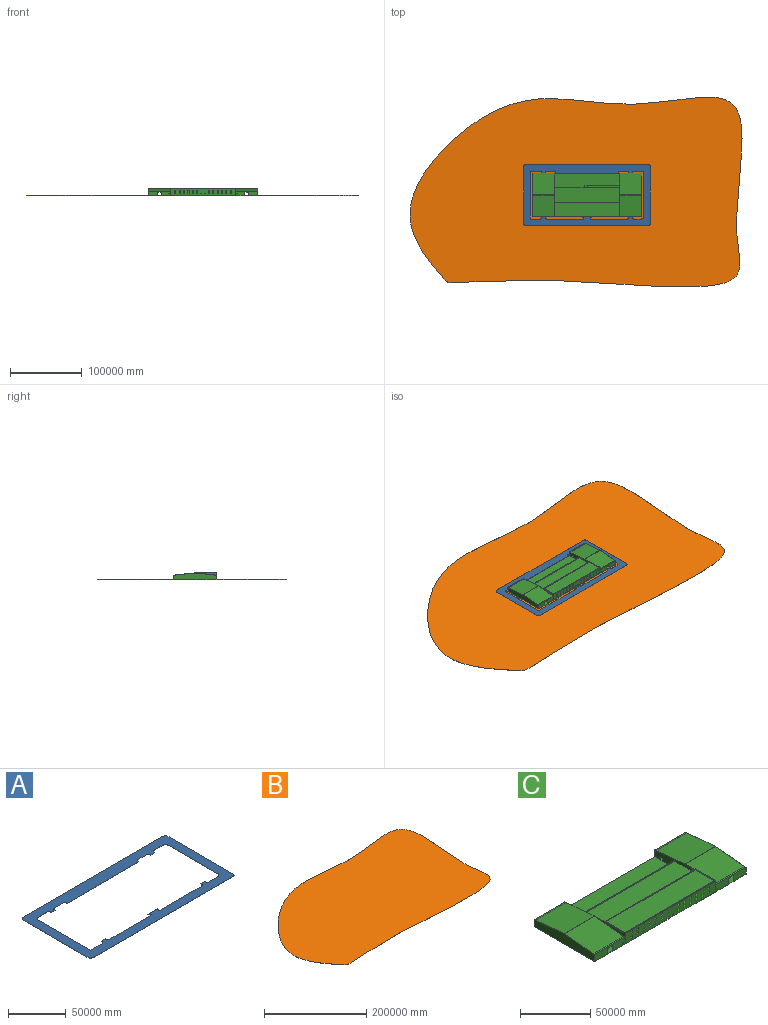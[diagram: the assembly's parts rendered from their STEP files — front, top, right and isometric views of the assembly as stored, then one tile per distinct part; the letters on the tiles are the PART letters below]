
ASSEMBLY  parts=3 mates=2
PART A: 50 faces, bbox 176784x85344x152.4 mm
  f0: plane 52273.2x152.4mm, normal (0,1,0), area 7966435.7mm2, adj f1,f47,f48,f49
  f1: cylinder r=3810mm len=3048mm, axis (0,0,-1), area 538428.4mm2, adj f0,f2,f48,f49
  f2: plane 12192x152.4mm, normal (0,1,0), area 1858060.8mm2, adj f1,f3,f48,f49
  f3: cylinder r=3810mm len=3048mm, axis (0,0,-1), area 538428.4mm2, adj f2,f4,f48,f49
  f4: plane 52273.2x152.4mm, normal (0,1,0), area 7966435.7mm2, adj f3,f5,f48,f49
  f5: plane 152.4x152.4mm, normal (1,0,0), area 23225.8mm2, adj f4,f6,f48,f49
  f6: extruded ~2895.6x1524mm, area 548894mm2, adj f5,f7,f48,f49
  f7: plane 152.4x152.4mm, normal (1,0,0), area 23225.8mm2, adj f6,f8,f48,f49
  f8: plane 4876.8x152.4mm, normal (0,1,0), area 743224.3mm2, adj f7,f9,f48,f49
  f9: plane 152.4x152.4mm, normal (-1,0,0), area 23225.8mm2, adj f8,f10,f48,f49
  f10: extruded ~2895.6x1524mm, area 548894mm2, adj f9,f11,f48,f49
  f11: plane 152.4x152.4mm, normal (-1,0,0), area 23225.8mm2, adj f10,f12,f48,f49
  f12: plane 14478x152.4mm, normal (0,1,0), area 2206447.2mm2, adj f11,f13,f48,f49
  f13: plane 63855.6x152.4mm, normal (1,0,0), area 9731593.4mm2, adj f12,f14,f48,f49
  f14: cylinder r=3048mm len=3048mm, axis (0,0,-1), area 729658.8mm2, adj f13,f15,f48,f49
  f15: plane 11430x152.4mm, normal (0,-1,0), area 1741932mm2, adj f14,f16,f48,f49
  f16: extruded ~2895.6x1524mm, area 548894mm2, adj f15,f17,f48,f49
  f17: plane 4876.8x152.4mm, normal (0,-1,0), area 743224.3mm2, adj f16,f18,f48,f49
  f18: extruded ~2895.6x1524mm, area 548894mm2, adj f17,f19,f48,f49
  f19: plane 11430x152.4mm, normal (0,-1,0), area 1741932mm2, adj f18,f20,f48,f49
  f20: extruded ~2895.6x1524mm, area 548894mm2, adj f19,f21,f48,f49
  f21: plane 87782.4x152.4mm, normal (0,-1,0), area 13378037.8mm2, adj f20,f22,f48,f49
  f22: extruded ~2895.6x1524mm, area 548894mm2, adj f21,f23,f48,f49
  f23: plane 11430x152.4mm, normal (0,-1,0), area 1741932mm2, adj f22,f24,f48,f49
  f24: extruded ~2895.6x1524mm, area 548894mm2, adj f23,f25,f48,f49
  f25: plane 4876.8x152.4mm, normal (0,-1,0), area 743224.3mm2, adj f24,f26,f48,f49
  f26: extruded ~2895.6x1524mm, area 548894mm2, adj f25,f27,f48,f49
  f27: plane 11430x152.4mm, normal (0,-1,0), area 1741932mm2, adj f26,f28,f48,f49
  f28: cylinder r=3048mm len=3048mm, axis (0,0,-1), area 729658.8mm2, adj f27,f29,f48,f49
  f29: plane 60655.2x152.4mm, normal (-1,0,0), area 9243852.5mm2, adj f28,f30,f48,f49
  f30: cylinder r=3048mm len=3048mm, axis (0,0,-1), area 729658.8mm2, adj f29,f31,f48,f49
  f31: plane 296.88x152.4mm, normal (-0.46,0.89,0), area 50857.4mm2, adj f30,f32,f48,f49
  f32: plane 11133.12x152.4mm, normal (0,1,0), area 1696687.8mm2, adj f31,f33,f48,f49
  f33: plane 152.4x152.4mm, normal (1,0,0), area 23225.8mm2, adj f32,f34,f48,f49
  f34: extruded ~2895.6x1524mm, area 548894mm2, adj f33,f35,f48,f49
  f35: plane 152.4x152.4mm, normal (1,0,0), area 23225.8mm2, adj f34,f36,f48,f49
  f36: plane 4876.8x152.4mm, normal (0,1,0), area 743224.3mm2, adj f35,f37,f48,f49
  f37: plane 152.4x152.4mm, normal (-1,0,0), area 23225.8mm2, adj f36,f38,f48,f49
  f38: extruded ~2895.6x1524mm, area 548894mm2, adj f37,f47,f48,f49
  f39: cylinder r=3048mm len=3048mm, axis (0,0,-1), area 729658.8mm2, adj f40,f46,f48,f49
  f40: plane 79248x152.4mm, normal (-1,0,0), area 12077395.2mm2, adj f39,f41,f48,f49
  f41: cylinder r=3048mm len=3048mm, axis (0,0,-1), area 729658.8mm2, adj f40,f42,f48,f49
  f42: plane 170688x152.4mm, normal (0,-1,0), area 26012851.2mm2, adj f41,f43,f48,f49
  f43: cylinder r=3048mm len=3048mm, axis (0,0,-1), area 729658.8mm2, adj f42,f44,f48,f49
  f44: plane 79248x152.4mm, normal (1,0,0), area 12077395.2mm2, adj f43,f45,f48,f49
  f45: cylinder r=3048mm len=3048mm, axis (0,0,-1), area 729658.8mm2, adj f44,f46,f48,f49
  f46: plane 170688x152.4mm, normal (0,1,0), area 26012851.2mm2, adj f39,f45,f48,f49
  f47: plane 152.4x152.4mm, normal (-1,0,0), area 23225.8mm2, adj f0,f38,f48,f49
  f48: plane 176784x85344mm, normal (0,0,1), area 4835317142.7mm2, adj f0,f1,f2,f3,f4,f5,f6,f7
  f49: plane 176784x85344mm, normal (0,0,-1), area 4835317142.7mm2, adj f0,f1,f2,f3,f4,f5,f6,f7
PART B: 3 faces, bbox 484095.1x286229.5x152.4 mm
  f0: extruded ~463355.35x265089.78mm, area 197646729.1mm2, adj f1,f2
  f1: plane 484095.12x286229.54mm, normal (0,0,1), area 107619152250.1mm2, adj f0
  f2: plane 484095.12x286229.54mm, normal (0,0,-1), area 107619152250.1mm2, adj f0
PART C: 253 faces, bbox 152400x60960x9906 mm
  f0: plane 30480x5943.6mm, normal (0,-1,0), area 158120974.1mm2, adj f3,f168,f172,f179,f250,f251,f252
  f1: plane 30480x5943.6mm, normal (0,-1,0), area 158120974.1mm2, adj f4,f169,f172,f177,f246,f247,f248
  f2: plane 40843.2x9144mm, normal (1,0,0), area 189846781.6mm2, adj f5,f8,f10,f12,f17,f18,f27,f28
  f3: plane 60655.2x8839.2mm, normal (-1,0,0), area 317727235.5mm2, adj f0,f6,f167,f171,f172,f173,f179,f180
  f4: plane 60655.2x8839.2mm, normal (1,0,0), area 317727235.5mm2, adj f1,f6,f170,f171,f172,f173,f174,f175
  f5: plane 90830.4x7010.4mm, normal (0,1,0), area 589934303.9mm2, adj f2,f13,f31,f35,f172,f184,f236,f237
  f6: plane 91135.2x5943.6mm, normal (0,-1,0), area 537769247mm2, adj f3,f4,f172,f173,f236,f237,f238
  f7: plane 90830.4x8991.6mm, normal (0,-1,0), area 784937785mm2, adj f12,f163,f164,f165,f166,f185,f186,f187
  f8: plane 91135.2x3657.6mm, normal (0,1,0), area 300680689mm2, adj f2,f10,f11,f12,f13,f24,f25,f40
  f9: plane 152400x9906mm, normal (0,-1,0), area 1161241548.5mm2, adj f17,f19,f20,f22,f23,f24,f25,f40
  f10: plane 30784.8x10515.6mm, normal (0,0,1), area 10939333mm2, adj f2,f8,f19,f20,f25,f28
  f11: plane 30784.8x10515.6mm, normal (0,0,1), area 10939333mm2, adj f8,f13,f21,f22,f23,f24
  f12: plane 90830.4x20878.8mm, normal (0,0,1), area 1882865911.7mm2, adj f2,f7,f8,f13,f34,f186,f187
  f13: plane 40843.2x9144mm, normal (-1,0,0), area 185666144.8mm2, adj f5,f8,f11,f12,f15,f16,f17,f18
  f14: plane 1516.38x152.4mm, normal (1,0,0), area 115548.2mm2, adj f15,f16,f21
  f15: plane 30784.8x6248.4mm, normal (0,1,0), area 163904188.3mm2, adj f13,f14,f16,f17,f21,f22,f246,f247
  f16: plane 1516.38x152.4mm, normal (0,0,1), area 231096.3mm2, adj f13,f14,f15,f21
  f17: plane 152400x60960mm, normal (0,0,-1), area 9272652422.4mm2, adj f2,f9,f13,f15,f18,f20,f22,f27
  f18: plane 90830.4x152.4mm, normal (0,1,0), area 13842553mm2, adj f2,f13,f17,f172
  f19: plane 30632.4x30327.6mm, normal (0,-0.1,0.99), area 933687222.9mm2, adj f9,f10,f20,f25
  f20: plane 60960x9144mm, normal (-1,0,0), area 464979715.2mm2, adj f9,f10,f17,f19,f27,f28
  f21: plane 30784.8x30327.6mm, normal (0,0.1,0.99), area 938100172.4mm2, adj f11,f13,f14,f15,f16,f22
  f22: plane 60960x9144mm, normal (1,0,0), area 464979715.2mm2, adj f9,f11,f15,f17,f21,f23
  f23: plane 30632.4x30327.6mm, normal (0,-0.1,0.99), area 933687222.9mm2, adj f9,f11,f22,f24
  f24: plane 30327.6x3810mm, normal (1,0,0), area 61548264mm2, adj f8,f9,f11,f23,f40
  f25: plane 30327.6x3810mm, normal (-1,0,0), area 61548264mm2, adj f8,f9,f10,f19,f40
  f26: plane 1516.38x152.4mm, normal (-1,0,0), area 115548.2mm2, adj f27,f28,f29
  f27: plane 30784.8x6248.4mm, normal (0,1,0), area 163904188.3mm2, adj f2,f17,f20,f26,f28,f29,f250,f251
  f28: plane 30784.8x30327.6mm, normal (0,0.1,0.99), area 938100172.4mm2, adj f2,f10,f20,f26,f27,f29
  f29: plane 1516.38x152.4mm, normal (0,0,1), area 231096.3mm2, adj f2,f26,f27,f28
  f30: plane 45415.2x914.4mm, normal (0,1,0), area 40134113.3mm2, adj f31,f33,f172,f184
  f31: plane 45415.2x3048mm, normal (0,0,1), area 138425529.6mm2, adj f5,f13,f30,f32,f184
  f32: plane 3048x3048mm, normal (0,0.29,0.96), area 9699362.1mm2, adj f13,f31,f33,f172
  f33: plane 3048x914.4mm, normal (-1,0,0), area 1393545.6mm2, adj f30,f32,f172
  f34: plane 90830.4x914.4mm, normal (0,-1,0), area 83055317.8mm2, adj f2,f12,f13,f35
  f35: plane 90830.4x152.4mm, normal (0,0,1), area 13842553mm2, adj f2,f5,f13,f34
  f36: plane 90525.6x609.6mm, normal (0,1,0), area 55184405.8mm2, adj f37,f39,f40,f41
  f37: plane 19507.2x609.6mm, normal (1,0,0), area 11891589.1mm2, adj f36,f38,f40,f41
  f38: plane 90525.6x609.6mm, normal (0,-1,0), area 55184405.8mm2, adj f37,f39,f40,f41
  f39: plane 19507.2x609.6mm, normal (-1,0,0), area 11891589.1mm2, adj f36,f38,f40,f41
  f40: plane 91135.2x20116.8mm, normal (0,0,1), area 67447607mm2, adj f8,f9,f24,f25,f36,f37,f38,f39
  f41: plane 90525.6x19507.2mm, normal (0,0,1), area 1765900984.3mm2, adj f36,f37,f38,f39
  f42: plane 4876.8x152.4mm, normal (-1,0,0), area 743224.3mm2, adj f9,f17,f43,f45,f170
  f43: plane 4876.8x152.4mm, normal (0,0,-1), area 743224.3mm2, adj f9,f42,f44,f170
  f44: plane 4876.8x152.4mm, normal (1,0,0), area 743224.3mm2, adj f9,f17,f43,f45,f170
  f45: plane 4876.8x152.4mm, normal (0,-1,0), area 743224.3mm2, adj f17,f42,f44,f172
  f46: plane 2133.6x152.4mm, normal (-1,0,0), area 325160.6mm2, adj f9,f17,f47,f49,f170
  f47: plane 914.4x152.4mm, normal (0,0,-1), area 139354.6mm2, adj f9,f46,f48,f170
  f48: plane 2133.6x152.4mm, normal (1,0,0), area 325160.6mm2, adj f9,f17,f47,f49,f170
  f49: plane 914.4x152.4mm, normal (0,-1,0), area 139354.6mm2, adj f17,f46,f48,f172
  f50: plane 2133.6x152.4mm, normal (1,0,0), area 325160.6mm2, adj f9,f17,f52,f53,f167
  f51: plane 2133.6x152.4mm, normal (-1,0,0), area 325160.6mm2, adj f9,f17,f52,f53,f167
  f52: plane 914.4x152.4mm, normal (0,0,-1), area 139354.6mm2, adj f9,f50,f51,f167
  f53: plane 914.4x152.4mm, normal (0,-1,0), area 139354.6mm2, adj f17,f50,f51,f172
  f54: plane 4876.8x152.4mm, normal (0,0,-1), area 743224.3mm2, adj f9,f55,f56,f167
  f55: plane 4876.8x152.4mm, normal (1,0,0), area 743224.3mm2, adj f9,f17,f54,f57,f167
  f56: plane 4876.8x152.4mm, normal (-1,0,0), area 743224.3mm2, adj f9,f17,f54,f57,f167
  f57: plane 4876.8x152.4mm, normal (0,-1,0), area 743224.3mm2, adj f17,f55,f56,f172
  f58: plane 2133.6x152.4mm, normal (1,0,0), area 325160.6mm2, adj f9,f17,f60,f61,f162
  f59: plane 2133.6x152.4mm, normal (-1,0,0), area 325160.6mm2, adj f9,f17,f60,f61,f162
  f60: plane 1828.8x152.4mm, normal (0,0,-1), area 278709.1mm2, adj f9,f58,f59,f162
  f61: plane 1828.8x152.4mm, normal (0,-1,0), area 278709.1mm2, adj f17,f58,f59,f163
  f62: plane 1524x152.4mm, normal (-1,0,0), area 232257.6mm2, adj f9,f63,f65,f162
  f63: plane 1524x152.4mm, normal (0,0,-1), area 232257.6mm2, adj f9,f62,f64,f162
  f64: plane 1524x152.4mm, normal (1,0,0), area 232257.6mm2, adj f9,f63,f65,f162
  f65: plane 1524x152.4mm, normal (0,0,1), area 232257.6mm2, adj f9,f62,f64,f162
  f66: plane 2133.6x152.4mm, normal (1,0,0), area 325160.6mm2, adj f9,f17,f68,f69,f162
  f67: plane 2133.6x152.4mm, normal (-1,0,0), area 325160.6mm2, adj f9,f17,f68,f69,f162
  f68: plane 1828.8x152.4mm, normal (0,0,-1), area 278709.1mm2, adj f9,f66,f67,f162
  f69: plane 1828.8x152.4mm, normal (0,-1,0), area 278709.1mm2, adj f17,f66,f67,f163
  f70: plane 1524x152.4mm, normal (1,0,0), area 232257.6mm2, adj f9,f71,f73,f162
  f71: plane 1524x152.4mm, normal (0,0,1), area 232257.6mm2, adj f9,f70,f72,f162
  f72: plane 1524x152.4mm, normal (-1,0,0), area 232257.6mm2, adj f9,f71,f73,f162
  f73: plane 1524x152.4mm, normal (0,0,-1), area 232257.6mm2, adj f9,f70,f72,f162
  f74: plane 1524x152.4mm, normal (1,0,0), area 232257.6mm2, adj f9,f75,f77,f162
  f75: plane 1524x152.4mm, normal (0,0,1), area 232257.6mm2, adj f9,f74,f76,f162
  f76: plane 1524x152.4mm, normal (-1,0,0), area 232257.6mm2, adj f9,f75,f77,f162
  f77: plane 1524x152.4mm, normal (0,0,-1), area 232257.6mm2, adj f9,f74,f76,f162
  f78: plane 1524x152.4mm, normal (0,0,1), area 232257.6mm2, adj f9,f79,f81,f162
  f79: plane 1524x152.4mm, normal (-1,0,0), area 232257.6mm2, adj f9,f78,f80,f162
  f80: plane 1524x152.4mm, normal (0,0,-1), area 232257.6mm2, adj f9,f79,f81,f162
  f81: plane 1524x152.4mm, normal (1,0,0), area 232257.6mm2, adj f9,f78,f80,f162
  f82: plane 1524x152.4mm, normal (0,0,1), area 232257.6mm2, adj f9,f83,f85,f162
  f83: plane 1524x152.4mm, normal (-1,0,0), area 232257.6mm2, adj f9,f82,f84,f162
  f84: plane 1524x152.4mm, normal (0,0,-1), area 232257.6mm2, adj f9,f83,f85,f162
  f85: plane 1524x152.4mm, normal (1,0,0), area 232257.6mm2, adj f9,f82,f84,f162
  f86: plane 1524x152.4mm, normal (-1,0,0), area 232257.6mm2, adj f9,f87,f89,f162
  f87: plane 1524x152.4mm, normal (0,0,-1), area 232257.6mm2, adj f9,f86,f88,f162
  f88: plane 1524x152.4mm, normal (1,0,0), area 232257.6mm2, adj f9,f87,f89,f162
  f89: plane 1524x152.4mm, normal (0,0,1), area 232257.6mm2, adj f9,f86,f88,f162
  f90: plane 1524x152.4mm, normal (1,0,0), area 232257.6mm2, adj f9,f91,f93,f162
  f91: plane 1524x152.4mm, normal (0,0,1), area 232257.6mm2, adj f9,f90,f92,f162
  f92: plane 1524x152.4mm, normal (-1,0,0), area 232257.6mm2, adj f9,f91,f93,f162
  f93: plane 1524x152.4mm, normal (0,0,-1), area 232257.6mm2, adj f9,f90,f92,f162
  f94: plane 1524x152.4mm, normal (0,0,1), area 232257.6mm2, adj f9,f95,f97,f162
  f95: plane 1524x152.4mm, normal (-1,0,0), area 232257.6mm2, adj f9,f94,f96,f162
  f96: plane 1524x152.4mm, normal (0,0,-1), area 232257.6mm2, adj f9,f95,f97,f162
  f97: plane 1524x152.4mm, normal (1,0,0), area 232257.6mm2, adj f9,f94,f96,f162
  f98: plane 1524x152.4mm, normal (-1,0,0), area 232257.6mm2, adj f9,f99,f101,f162
  f99: plane 1524x152.4mm, normal (0,0,-1), area 232257.6mm2, adj f9,f98,f100,f162
  f100: plane 1524x152.4mm, normal (1,0,0), area 232257.6mm2, adj f9,f99,f101,f162
  f101: plane 1524x152.4mm, normal (0,0,1), area 232257.6mm2, adj f9,f98,f100,f162
  f102: plane 1524x152.4mm, normal (0,0,-1), area 232257.6mm2, adj f9,f103,f105,f162
  f103: plane 1524x152.4mm, normal (1,0,0), area 232257.6mm2, adj f9,f102,f104,f162
  f104: plane 1524x152.4mm, normal (0,0,1), area 232257.6mm2, adj f9,f103,f105,f162
  f105: plane 1524x152.4mm, normal (-1,0,0), area 232257.6mm2, adj f9,f102,f104,f162
  f106: plane 1524x152.4mm, normal (0,0,1), area 232257.6mm2, adj f9,f107,f109,f162
  f107: plane 1524x152.4mm, normal (-1,0,0), area 232257.6mm2, adj f9,f106,f108,f162
  f108: plane 1524x152.4mm, normal (0,0,-1), area 232257.6mm2, adj f9,f107,f109,f162
  f109: plane 1524x152.4mm, normal (1,0,0), area 232257.6mm2, adj f9,f106,f108,f162
  f110: plane 1524x152.4mm, normal (1,0,0), area 232257.6mm2, adj f9,f111,f113,f162
  f111: plane 1524x152.4mm, normal (0,0,1), area 232257.6mm2, adj f9,f110,f112,f162
  f112: plane 1524x152.4mm, normal (-1,0,0), area 232257.6mm2, adj f9,f111,f113,f162
  f113: plane 1524x152.4mm, normal (0,0,-1), area 232257.6mm2, adj f9,f110,f112,f162
  f114: plane 1524x152.4mm, normal (1,0,0), area 232257.6mm2, adj f9,f115,f117,f162
  f115: plane 1524x152.4mm, normal (0,0,1), area 232257.6mm2, adj f9,f114,f116,f162
  f116: plane 1524x152.4mm, normal (-1,0,0), area 232257.6mm2, adj f9,f115,f117,f162
  f117: plane 1524x152.4mm, normal (0,0,-1), area 232257.6mm2, adj f9,f114,f116,f162
  f118: plane 1524x152.4mm, normal (1,0,0), area 232257.6mm2, adj f9,f119,f121,f162
  f119: plane 1524x152.4mm, normal (0,0,1), area 232257.6mm2, adj f9,f118,f120,f162
  f120: plane 1524x152.4mm, normal (-1,0,0), area 232257.6mm2, adj f9,f119,f121,f162
  f121: plane 1524x152.4mm, normal (0,0,-1), area 232257.6mm2, adj f9,f118,f120,f162
  f122: plane 1524x152.4mm, normal (1,0,0), area 232257.6mm2, adj f9,f123,f125,f162
  f123: plane 1524x152.4mm, normal (0,0,1), area 232257.6mm2, adj f9,f122,f124,f162
  f124: plane 1524x152.4mm, normal (-1,0,0), area 232257.6mm2, adj f9,f123,f125,f162
  f125: plane 1524x152.4mm, normal (0,0,-1), area 232257.6mm2, adj f9,f122,f124,f162
  f126: plane 1524x152.4mm, normal (1,0,0), area 232257.6mm2, adj f9,f127,f129,f162
  f127: plane 1524x152.4mm, normal (0,0,1), area 232257.6mm2, adj f9,f126,f128,f162
  f128: plane 1524x152.4mm, normal (-1,0,0), area 232257.6mm2, adj f9,f127,f129,f162
  f129: plane 1524x152.4mm, normal (0,0,-1), area 232257.6mm2, adj f9,f126,f128,f162
  f130: plane 1524x152.4mm, normal (1,0,0), area 232257.6mm2, adj f9,f131,f133,f162
  f131: plane 1524x152.4mm, normal (0,0,1), area 232257.6mm2, adj f9,f130,f132,f162
  f132: plane 1524x152.4mm, normal (-1,0,0), area 232257.6mm2, adj f9,f131,f133,f162
  f133: plane 1524x152.4mm, normal (0,0,-1), area 232257.6mm2, adj f9,f130,f132,f162
  f134: plane 1524x152.4mm, normal (0,0,-1), area 232257.6mm2, adj f9,f135,f137,f162
  f135: plane 1524x152.4mm, normal (1,0,0), area 232257.6mm2, adj f9,f134,f136,f162
  f136: plane 1524x152.4mm, normal (0,0,1), area 232257.6mm2, adj f9,f135,f137,f162
  f137: plane 1524x152.4mm, normal (-1,0,0), area 232257.6mm2, adj f9,f134,f136,f162
  f138: plane 1524x152.4mm, normal (1,0,0), area 232257.6mm2, adj f9,f139,f141,f162
  f139: plane 1524x152.4mm, normal (0,0,1), area 232257.6mm2, adj f9,f138,f140,f162
  f140: plane 1524x152.4mm, normal (-1,0,0), area 232257.6mm2, adj f9,f139,f141,f162
  f141: plane 1524x152.4mm, normal (0,0,-1), area 232257.6mm2, adj f9,f138,f140,f162
  f142: plane 1524x152.4mm, normal (0,0,-1), area 232257.6mm2, adj f9,f143,f145,f162
  f143: plane 1524x152.4mm, normal (1,0,0), area 232257.6mm2, adj f9,f142,f144,f162
  f144: plane 1524x152.4mm, normal (0,0,1), area 232257.6mm2, adj f9,f143,f145,f162
  f145: plane 1524x152.4mm, normal (-1,0,0), area 232257.6mm2, adj f9,f142,f144,f162
  f146: plane 1524x152.4mm, normal (0,0,-1), area 232257.6mm2, adj f9,f147,f149,f162
  f147: plane 1524x152.4mm, normal (1,0,0), area 232257.6mm2, adj f9,f146,f148,f162
  f148: plane 1524x152.4mm, normal (0,0,1), area 232257.6mm2, adj f9,f147,f149,f162
  f149: plane 1524x152.4mm, normal (-1,0,0), area 232257.6mm2, adj f9,f146,f148,f162
  f150: plane 1524x152.4mm, normal (0,0,-1), area 232257.6mm2, adj f9,f151,f153,f162
  f151: plane 1524x152.4mm, normal (1,0,0), area 232257.6mm2, adj f9,f150,f152,f162
  f152: plane 1524x152.4mm, normal (0,0,1), area 232257.6mm2, adj f9,f151,f153,f162
  f153: plane 1524x152.4mm, normal (-1,0,0), area 232257.6mm2, adj f9,f150,f152,f162
  f154: plane 1524x152.4mm, normal (-1,0,0), area 232257.6mm2, adj f9,f155,f157,f162
  f155: plane 1524x152.4mm, normal (0,0,-1), area 232257.6mm2, adj f9,f154,f156,f162
  f156: plane 1524x152.4mm, normal (1,0,0), area 232257.6mm2, adj f9,f155,f157,f162
  f157: plane 1524x152.4mm, normal (0,0,1), area 232257.6mm2, adj f9,f154,f156,f162
  f158: plane 1524x152.4mm, normal (-1,0,0), area 232257.6mm2, adj f9,f159,f161,f162
  f159: plane 1524x152.4mm, normal (0,0,-1), area 232257.6mm2, adj f9,f158,f160,f162
  f160: plane 1524x152.4mm, normal (1,0,0), area 232257.6mm2, adj f9,f159,f161,f162
  f161: plane 1524x152.4mm, normal (0,0,1), area 232257.6mm2, adj f9,f158,f160,f162
  f162: plane 90830.4x8991.6mm, normal (0,1,0), area 753722363.5mm2, adj f58,f59,f60,f62,f63,f64,f65,f66
  f163: plane 90830.4x19812mm, normal (0,0,1), area 1799531884.8mm2, adj f7,f61,f69,f162,f164,f165
  f164: plane 19812x8991.6mm, normal (-1,0,0), area 178141579.2mm2, adj f7,f162,f163,f166
  f165: plane 19812x8991.6mm, normal (1,0,0), area 178141579.2mm2, adj f7,f162,f163,f166
  f166: plane 90830.4x19812mm, normal (0,0,-1), area 1799531884.8mm2, adj f7,f162,f164,f165
  f167: plane 30480x5943.6mm, normal (0,1,0), area 156309364.8mm2, adj f3,f50,f51,f52,f54,f55,f56,f168
  f168: plane 60655.2x8839.2mm, normal (1,0,0), area 444818594.2mm2, adj f0,f167,f172,f179,f180,f181,f182,f183
  f169: plane 60655.2x8839.2mm, normal (-1,0,0), area 444818594.2mm2, adj f1,f170,f172,f174,f175,f176,f177,f178
  f170: plane 30480x5943.6mm, normal (0,1,0), area 156309364.8mm2, adj f4,f42,f43,f44,f46,f47,f48,f169
  f171: plane 91135.2x5943.6mm, normal (0,1,0), area 541671174.7mm2, adj f3,f4,f172,f173
  f172: plane 152095.2x60655.2mm, normal (0,0,1), area 7229807475.8mm2, adj f0,f1,f2,f3,f4,f5,f6,f13
  f173: plane 91135.2x20726.4mm, normal (0,0,-1), area 1888904609.3mm2, adj f3,f4,f6,f171
  f174: plane 30480x304.8mm, normal (0,0,-1), area 9290304mm2, adj f4,f169,f176,f178
  f175: plane 30480x1363.98mm, normal (0,0,-1), area 41574110.4mm2, adj f4,f169,f170,f176
  f176: plane 30480x28811.22mm, normal (0,0.1,-0.99), area 882589912.2mm2, adj f4,f169,f174,f175
  f177: plane 30480x1363.98mm, normal (0,0,-1), area 41574110.4mm2, adj f1,f4,f169,f178
  f178: plane 30480x28811.22mm, normal (0,-0.1,-0.99), area 882589912.2mm2, adj f4,f169,f174,f177
  f179: plane 30480x1363.98mm, normal (0,0,-1), area 41574110.4mm2, adj f0,f3,f168,f181
  f180: plane 30480x304.8mm, normal (0,0,-1), area 9290304mm2, adj f3,f168,f181,f182
  f181: plane 30480x28811.22mm, normal (0,-0.1,-0.99), area 882589912.2mm2, adj f3,f168,f179,f180
  f182: plane 30480x28811.22mm, normal (0,0.1,-0.99), area 882589912.2mm2, adj f3,f168,f180,f183
  f183: plane 30480x1363.98mm, normal (0,0,-1), area 41574110.4mm2, adj f3,f167,f168,f182
  f184: plane 3048x3048mm, normal (-0.29,0,0.96), area 9699362.1mm2, adj f5,f30,f31,f172
  f185: plane 1828.8x152.4mm, normal (0,0,-1), area 278709.1mm2, adj f7,f8,f186,f187
  f186: plane 2133.6x152.4mm, normal (-1,0,0), area 325160.6mm2, adj f7,f8,f12,f185
  f187: plane 2133.6x152.4mm, normal (1,0,0), area 325160.6mm2, adj f7,f8,f12,f185
  f188: plane 1524x152.4mm, normal (0,0,1), area 232257.6mm2, adj f7,f8,f189,f191
  f189: plane 1524x152.4mm, normal (1,0,0), area 232257.6mm2, adj f7,f8,f188,f190
  f190: plane 1524x152.4mm, normal (0,0,-1), area 232257.6mm2, adj f7,f8,f189,f191
  f191: plane 1524x152.4mm, normal (-1,0,0), area 232257.6mm2, adj f7,f8,f188,f190
  f192: plane 1524x152.4mm, normal (1,0,0), area 232257.6mm2, adj f7,f8,f193,f195
  f193: plane 1524x152.4mm, normal (0,0,-1), area 232257.6mm2, adj f7,f8,f192,f194
  f194: plane 1524x152.4mm, normal (-1,0,0), area 232257.6mm2, adj f7,f8,f193,f195
  f195: plane 1524x152.4mm, normal (0,0,1), area 232257.6mm2, adj f7,f8,f192,f194
  f196: plane 1524x152.4mm, normal (1,0,0), area 232257.6mm2, adj f7,f8,f197,f199
  f197: plane 1524x152.4mm, normal (0,0,-1), area 232257.6mm2, adj f7,f8,f196,f198
  f198: plane 1524x152.4mm, normal (-1,0,0), area 232257.6mm2, adj f7,f8,f197,f199
  f199: plane 1524x152.4mm, normal (0,0,1), area 232257.6mm2, adj f7,f8,f196,f198
  f200: plane 1524x152.4mm, normal (0,0,1), area 232257.6mm2, adj f7,f8,f201,f203
  f201: plane 1524x152.4mm, normal (1,0,0), area 232257.6mm2, adj f7,f8,f200,f202
  f202: plane 1524x152.4mm, normal (0,0,-1), area 232257.6mm2, adj f7,f8,f201,f203
  f203: plane 1524x152.4mm, normal (-1,0,0), area 232257.6mm2, adj f7,f8,f200,f202
  f204: plane 1524x152.4mm, normal (0,0,-1), area 232257.6mm2, adj f7,f8,f205,f207
  f205: plane 1524x152.4mm, normal (-1,0,0), area 232257.6mm2, adj f7,f8,f204,f206
  f206: plane 1524x152.4mm, normal (0,0,1), area 232257.6mm2, adj f7,f8,f205,f207
  f207: plane 1524x152.4mm, normal (1,0,0), area 232257.6mm2, adj f7,f8,f204,f206
  f208: plane 1524x152.4mm, normal (1,0,0), area 232257.6mm2, adj f7,f8,f209,f211
  f209: plane 1524x152.4mm, normal (0,0,-1), area 232257.6mm2, adj f7,f8,f208,f210
  f210: plane 1524x152.4mm, normal (-1,0,0), area 232257.6mm2, adj f7,f8,f209,f211
  f211: plane 1524x152.4mm, normal (0,0,1), area 232257.6mm2, adj f7,f8,f208,f210
  f212: plane 1524x152.4mm, normal (1,0,0), area 232257.6mm2, adj f7,f8,f213,f215
  f213: plane 1524x152.4mm, normal (0,0,-1), area 232257.6mm2, adj f7,f8,f212,f214
  f214: plane 1524x152.4mm, normal (-1,0,0), area 232257.6mm2, adj f7,f8,f213,f215
  f215: plane 1524x152.4mm, normal (0,0,1), area 232257.6mm2, adj f7,f8,f212,f214
  f216: plane 1524x152.4mm, normal (1,0,0), area 232257.6mm2, adj f7,f8,f217,f219
  f217: plane 1524x152.4mm, normal (0,0,-1), area 232257.6mm2, adj f7,f8,f216,f218
  f218: plane 1524x152.4mm, normal (-1,0,0), area 232257.6mm2, adj f7,f8,f217,f219
  f219: plane 1524x152.4mm, normal (0,0,1), area 232257.6mm2, adj f7,f8,f216,f218
  f220: plane 1524x152.4mm, normal (1,0,0), area 232257.6mm2, adj f7,f8,f221,f223
  f221: plane 1524x152.4mm, normal (0,0,-1), area 232257.6mm2, adj f7,f8,f220,f222
  f222: plane 1524x152.4mm, normal (-1,0,0), area 232257.6mm2, adj f7,f8,f221,f223
  f223: plane 1524x152.4mm, normal (0,0,1), area 232257.6mm2, adj f7,f8,f220,f222
  f224: plane 1524x152.4mm, normal (1,0,0), area 232257.6mm2, adj f7,f8,f225,f227
  f225: plane 1524x152.4mm, normal (0,0,-1), area 232257.6mm2, adj f7,f8,f224,f226
  f226: plane 1524x152.4mm, normal (-1,0,0), area 232257.6mm2, adj f7,f8,f225,f227
  f227: plane 1524x152.4mm, normal (0,0,1), area 232257.6mm2, adj f7,f8,f224,f226
  f228: plane 1524x152.4mm, normal (0,0,1), area 232257.6mm2, adj f7,f8,f229,f231
  f229: plane 1524x152.4mm, normal (1,0,0), area 232257.6mm2, adj f7,f8,f228,f230
  f230: plane 1524x152.4mm, normal (0,0,-1), area 232257.6mm2, adj f7,f8,f229,f231
  f231: plane 1524x152.4mm, normal (-1,0,0), area 232257.6mm2, adj f7,f8,f228,f230
  f232: plane 1524x152.4mm, normal (0,0,1), area 232257.6mm2, adj f7,f8,f233,f235
  f233: plane 1524x152.4mm, normal (1,0,0), area 232257.6mm2, adj f7,f8,f232,f234
  f234: plane 1524x152.4mm, normal (0,0,-1), area 232257.6mm2, adj f7,f8,f233,f235
  f235: plane 1524x152.4mm, normal (-1,0,0), area 232257.6mm2, adj f7,f8,f232,f234
  f236: plane 2133.6x152.4mm, normal (-1,0,0), area 325160.6mm2, adj f5,f6,f172,f238
  f237: plane 2133.6x152.4mm, normal (1,0,0), area 325160.6mm2, adj f5,f6,f172,f238
  f238: plane 1828.8x152.4mm, normal (0,0,-1), area 278709.1mm2, adj f5,f6,f236,f237
  f239: plane 2133.6x152.4mm, normal (0,-1,0), area 325160.6mm2, adj f4,f13,f172,f241
  f240: plane 2133.6x152.4mm, normal (0,1,0), area 325160.6mm2, adj f4,f13,f172,f241
  f241: plane 1828.8x152.4mm, normal (0,0,-1), area 278709.1mm2, adj f4,f13,f239,f240
  f242: plane 1828.8x152.4mm, normal (0,0,-1), area 278709.1mm2, adj f2,f3,f243,f244
  f243: plane 2133.6x152.4mm, normal (0,1,0), area 325160.6mm2, adj f2,f3,f172,f242
  f244: plane 2133.6x152.4mm, normal (0,-1,0), area 325160.6mm2, adj f2,f3,f172,f242
  f245: plane 4876.8x152.4mm, normal (0,1,0), area 743224.3mm2, adj f17,f172,f247,f248
  f246: plane 4876.8x152.4mm, normal (0,0,-1), area 743224.3mm2, adj f1,f15,f247,f248
  f247: plane 4876.8x152.4mm, normal (-1,0,0), area 743224.3mm2, adj f1,f15,f17,f245,f246
  f248: plane 4876.8x152.4mm, normal (1,0,0), area 743224.3mm2, adj f1,f15,f17,f245,f246
  f249: plane 4876.8x152.4mm, normal (0,1,0), area 743224.3mm2, adj f17,f172,f251,f252
  f250: plane 4876.8x152.4mm, normal (0,0,-1), area 743224.3mm2, adj f0,f27,f251,f252
  f251: plane 4876.8x152.4mm, normal (-1,0,0), area 743224.3mm2, adj f0,f17,f27,f249,f250
  f252: plane 4876.8x152.4mm, normal (1,0,0), area 743224.3mm2, adj f0,f17,f27,f249,f250
PLACE A t=(-5235.66,16917.48,-4271.79)mm
PLACE B t=(6389.48,60845.21,7767.81)mm
PLACE C t=(-5235.66,17069.88,-4271.79)mm fixed
MATE fastened A.f21 <-> C.f18  axis (0,-1,0) through (-5235.66,47397.48,-4195.59)mm
MATE fastened B.f1 <-> C.f17  axis (0,0,1) through (-5235.66,17027.23,-4271.79)mm
